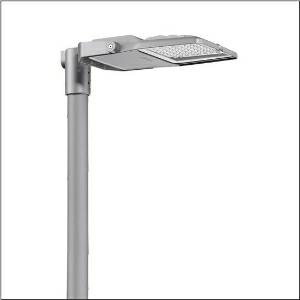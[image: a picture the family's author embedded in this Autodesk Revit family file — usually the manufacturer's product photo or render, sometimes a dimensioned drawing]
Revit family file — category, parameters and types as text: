
# Revit family: floodlight_fl_21_iq_mini___pl52_5xa7772b2d3a_55c6
name_source: partatom
category: Lighting Fixtures
units: mm (PartAtom-declared; Revit-internal decimal feet)

## family parameters
Cut with Voids When Loaded = No
Host = Face
Light Source = No
Part Type = Normal
Room Calculation Point = No
Round Connector Dimension = Use Diameter
Shared = No

## types (1)
- --- (1 x LED, 6240 lm, 45.5 W, 3000K)
    Apparent Load = 46 VA
    CIE Flux Codes = 26 60 98 100 100
    Color Rendering = 70
    Color Temperature = 3000K
    Default Elevation = 1800 mm
    Description = Floodlight FL 21 iQ mini, floodlight, primary light control with lens, of PMMA, primary optical cover: protective disc, of toughened safety glass, transparent, light distribution: PL52, light emission: direct distribution, installation type: surface-mounted, lamps: LED, High Power LED, rated values: 6.240lm | 45,5W | 137,1lm/W (begin service life); end service life: 6.240lm | 48W; at 50% lumin. flux: 3.120lm | 21,5W | 145,1lm/W, colour temperature: 3000K, colour rendering: CRI > 70, light colour: 730, light setting 1 begin service life: 100% | 6.240lm | 45,5W | 137,1lm/W | 3.000K, light setting 1 end service life: 48W, further light settings possible, control: pre-setting: linear dimming characteristic, Auto-Match, Temp-Guard, Night-Set, Smart-Wire, Desk-Remote (wireless, voltage-free reading and setting of iQ features in the workshop via application-optimized NFC function/RFID function), optimised constant luminous flux control (CLO 2.0), Light-Fading, Lumen-Switch, with terminal, 6-pole, mains connection: 220..240V, AC, 50/60Hz, luminaire housing, of diecast aluminium, powder-coated, SITECO metallic grey (DB 702S), corrosivity category C5 mid according to DIN EN ISO 12944suitable for swimming poolschlorine-resistant, sealing non-destructively replaceable, please order mast flange separately, mast bracket, of steel, galvanised, powder-coated, protection rating (complete): IP66, insulation class (complete): insulation class II (safety insulation), certification: CE, ENEC, VDE, protection symbol: D, impact resistance: IK08, permissible operating ambient temperature: -40..+40°C, permissible operating ambient temperature for outdoor applications: -40..+50°C, standard: DIN EN 12944, LABS conformity tested according to VDMA 24364:2018-05, packaging unit: 1 piece

Light Distribution: PL52
    Height = 70 mm
    Lamp = 1 x LED
    Lamp Light Flux = 6240 lm
    Lamp Power = 45.5 W
    Lamp count = 1
    Length = 485 mm
    Luminous efficacy = 137 lm/W
    Manufacturer = Siteco
    ModVariant = No
    Model = 5XA7772B2D3A
    Number of Poles = 1
    OnlyDefault = Yes
    Power Factor = 1
    Product Name = Floodlight FL 21 iQ mini | PL52
    Product group = floodlight | pylon annexe
    ProductGroupID = 6201
    Protection Class = Protection class II
    Protection Degree = IP 66
    RLX_Detail_Level = 1
    RLX_Emergency_Light_Flux = 0 lm
    RLX_Emergency_Type = 0
    RLX_Emergency_Type_DB = No
    RlxData = <blob elided: 101557 chars, md5=c02d1f30>
    Socket = socket
    Standby Power = 0 W
    System Light Flux = 6240 lm
    System Power = 46 W
    Type Comments = factory setting: luminous flux: 100 % | dim-lin: 254 | 463 mA
    Type Image = l_1007125.jpg
    URL = http://relux.com
    VarID = @adj_164313
    Voltage = 0 V
    Weight = 0.00 kg
    Width = 337 mm

## geometry (parser evidence)
native form markers: Blend x4, Sweep x13
no freeform markers — native parametric forms only
